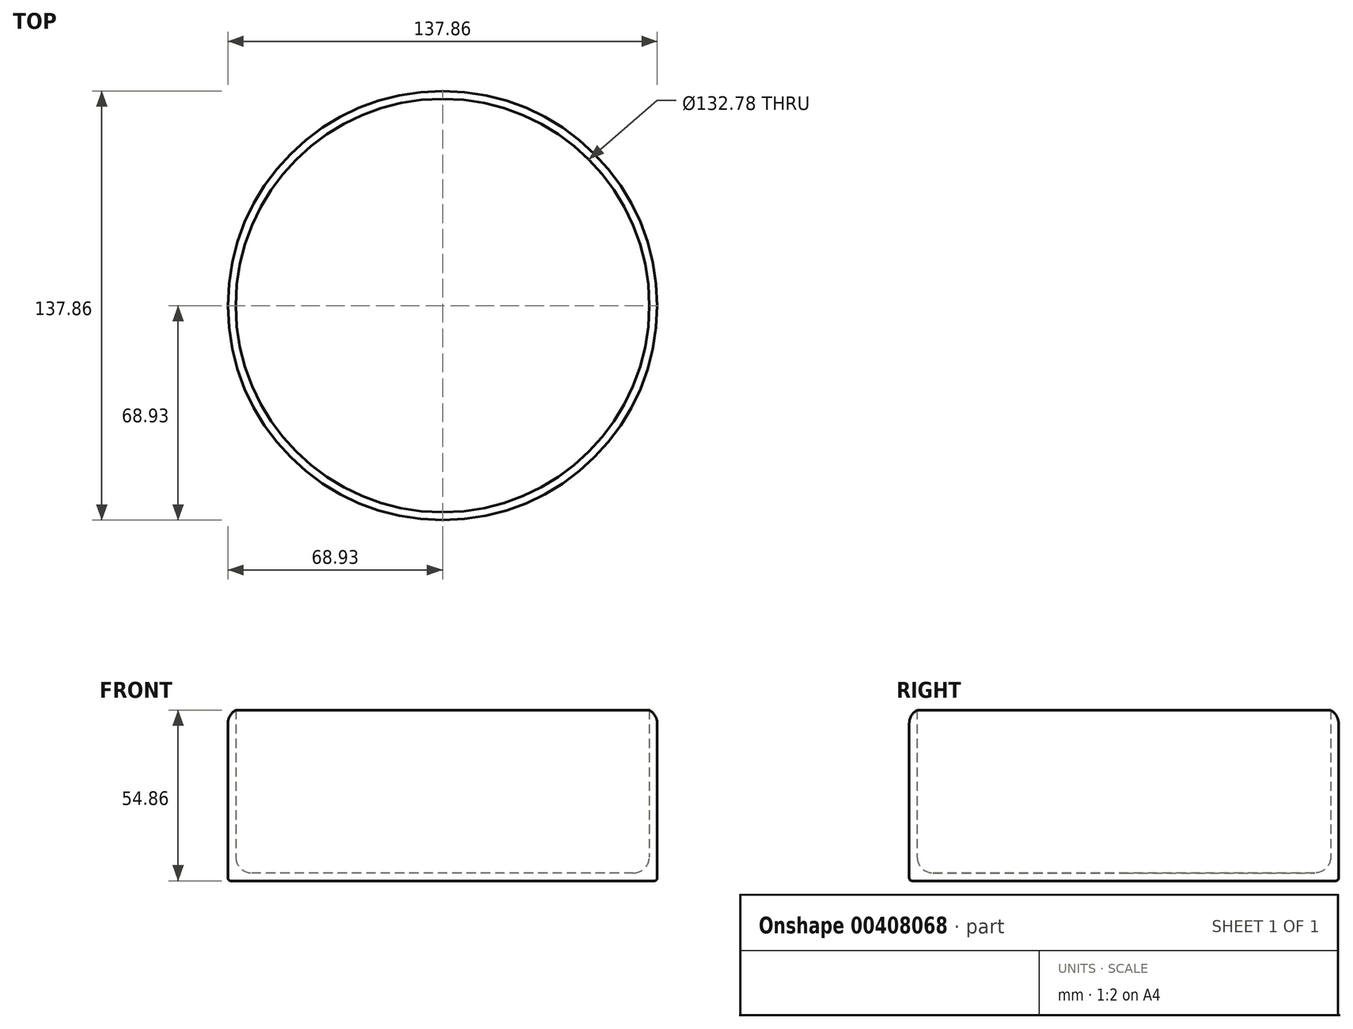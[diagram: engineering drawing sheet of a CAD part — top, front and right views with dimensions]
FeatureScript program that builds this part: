
annotation { "Feature Type Name" : "Feature", "Feature Type Description" : "" }
export const myFeature = defineFeature(function(context is Context, id is Id, definition is map)
    precondition{}
    {
        {
            var Q0;
            Q0=qCreatedBy(makeId("Top.planeOp"),FACE);
            var sketch = newSketch(context, id + "F0", { "sketchPlane" : qUnion([Q0])});
            skCircle(sketch, "E0.0", {"center": v(0, 0) * mm, "radius": 68.93 * mm});
            skSolve(sketch);
        }
        {
            var Q0;
            Q0=makeQuery(id+"F0.imprint","IMPRINT",FACE,{"disambiguationData":[TD([[makeQuery(id+"F0.imprint","IMPRINT",EDGE,{"derivedFrom":sQuery(id+"F0.wireOp",EDGE,"E0.0")}),1.0]])]});
            extrude(context, id + "F1", {"entities" : qUnion([Q0]), "depth" : 54.86 * mm});
        }
        {
            var Q0;
            Q0=makeQuery(id+"F1.opExtrude","CAP_FACE",FACE,{"disambiguationData":[OSD([sQuery(id+"F0.wireOp",EDGE,"E0.0")])],"isStart":false});
            shell(context, id + "F2", {"entities" : qUnion([Q0]), "thickness" : 2.54 * mm});
        }
        {
            var Q0;
            Q0=makeQuery(id+"F1.opExtrude","CAP_EDGE",EDGE,{"disambiguationData":[OSD([sQuery(id+"F0.wireOp",EDGE,"E0.0")])],"isStart":false});
            fillet(context, id + "F3", {"entities" : qUnion([Q0]), "radius" : 5.08 * mm, "tangentPropagation" : true, "allowEdgeOverflow" : false});
        }
        {
            var Q0;
            Q0=makeQuery(id+"F1.opExtrude","CAP_EDGE",EDGE,{"disambiguationData":[OSD([sQuery(id+"F0.wireOp",EDGE,"E0.0")])],"isStart":true});
            fillet(context, id + "F4", {"entities" : qUnion([Q0]), "radius" : 0.9 * mm, "tangentPropagation" : true, "allowEdgeOverflow" : false});
        }
        {
            var Q0;
            {var subQ0=sQuery(id+"F0.wireOp",EDGE,"E0.0");Q0=makeQuery(id+"F2.opShell","OFFSET_EDGE",EDGE,{"disambiguationData":[OSD([subQ0]),TDD([makeQuery(id+"F1.opExtrude","CAP_EDGE",EDGE,{"disambiguationData":[OSD([subQ0])],"isStart":true})])]});}
            fillet(context, id + "F5", {"entities" : qUnion([Q0]), "radius" : 5.08 * mm, "tangentPropagation" : true, "allowEdgeOverflow" : false});
        }
    });
